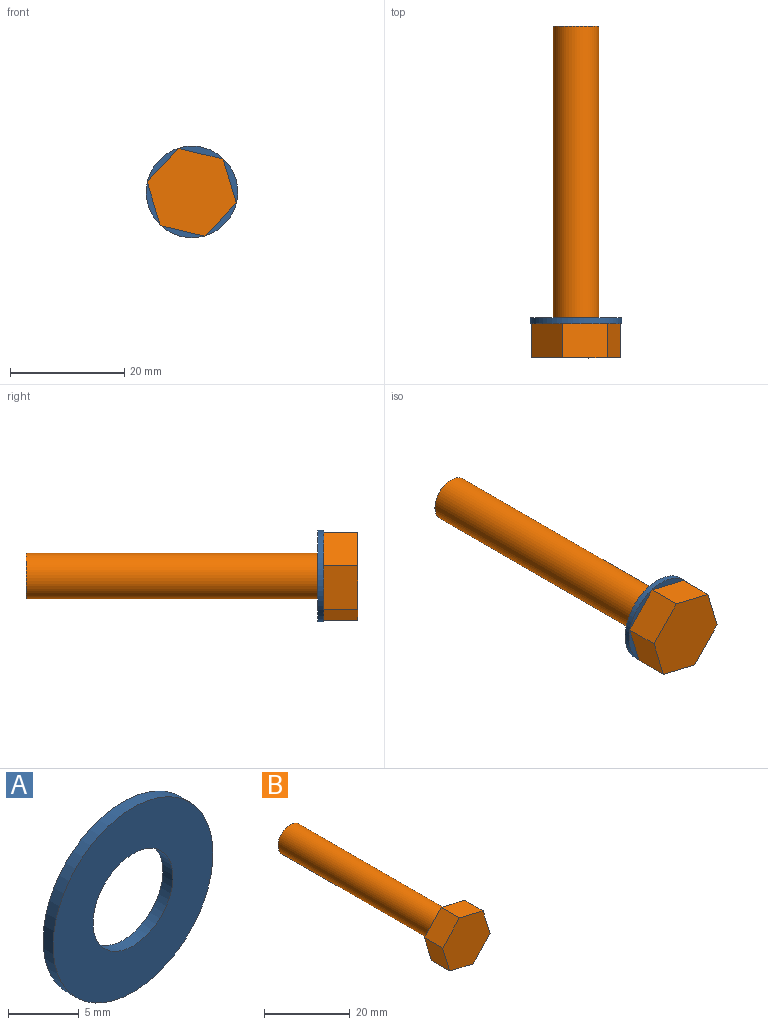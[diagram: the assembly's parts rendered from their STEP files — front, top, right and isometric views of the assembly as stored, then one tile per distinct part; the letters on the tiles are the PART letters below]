
ASSEMBLY  parts=2 mates=1
PART A: 4 faces, bbox 16x1x16 mm
  f0: cylinder r=4mm len=8mm, axis (0,-1,0), area 25.1mm2, adj f2,f3
  f1: cylinder r=8mm len=16mm, axis (0,-1,0), area 50.3mm2, adj f2,f3
  f2: plane 16x16mm, normal (0,1,0), area 150.8mm2, adj f0,f1
  f3: plane 16x16mm, normal (0,-1,0), area 150.8mm2, adj f0,f1
PART B: 10 faces, bbox 15.6x58x15.3 mm
  f0: plane 7.67x6mm, normal (0.96,0,0.29), area 48mm2, adj f1,f5,f6,f7
  f1: plane 7.78x6mm, normal (0.23,0,0.97), area 48mm2, adj f0,f2,f6,f7
  f2: plane 6x5.81mm, normal (-0.73,0,0.69), area 48mm2, adj f1,f3,f6,f7
  f3: plane 7.67x6mm, normal (-0.96,0,-0.29), area 48mm2, adj f2,f4,f6,f7
  f4: plane 7.78x6mm, normal (-0.23,0,-0.97), area 48mm2, adj f3,f5,f6,f7
  f5: plane 6x5.81mm, normal (0.73,0,-0.69), area 48mm2, adj f0,f4,f6,f7
  f6: plane 15.56x15.33mm, normal (0,-1,0), area 166.3mm2, adj f0,f1,f2,f3,f4,f5
  f7: plane 15.56x15.33mm, normal (0,1,0), area 116mm2, adj f0,f1,f2,f3,f4,f5,f8
  f8: cylinder r=4mm len=52mm, axis (0,-1,0), area 1306.9mm2, adj f7,f9
  f9: plane 8x8mm, normal (0,1,0), area 50.3mm2, adj f8
PLACE A at identity
PLACE B t=(14.82,0,66.88)mm
MATE fastened B.f8 <-> A.f0  axis (0,-1,0) through (75.4,0,173.59)mm
